AUTODESK INVENTOR PART (.ipt)
format: ipt  version: 2018 (Build 220112000, 112)  size: 163,328 bytes
history: native  units: in
note: dims shown in document units (in); Inventor stores cm internally (conversion verified against a paired STEP export)
features: other x3, reference x2, plane x1, extrude x1, sketch x1
ambient origin geometry x8: Origin, YZ Plane, XZ Plane, XY Plane, X Axis, Y Axis, Z Axis, Center Point
bodies: Solid1 (feature_tree)
feature tree (8):
  plane  "Work Plane1"
  extrude  "Extrusion1"  Depth=120.0in TaperAngle=360.0deg
  sketch  "Sketch1"  dims[d0=0.0309in d1=15.748in d3=360.0deg d5=120.0in d6=0.0in]
  reference  "Reference1"
  reference  "Reference2"
  other  "FullWheelWeek3AJB.iam"
  other  "WheelAJB:2"
  other  "WheelAJB:1"
